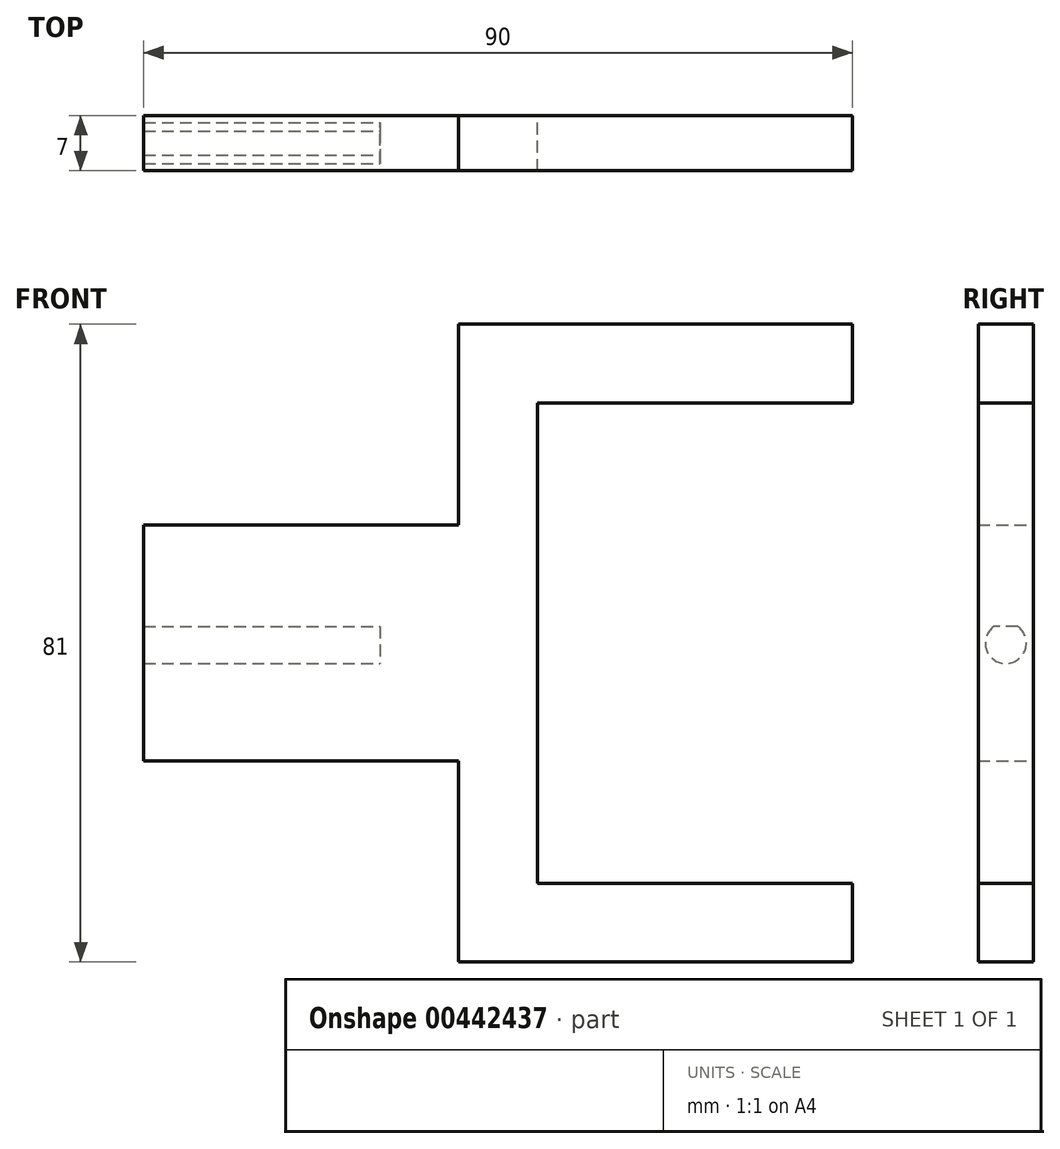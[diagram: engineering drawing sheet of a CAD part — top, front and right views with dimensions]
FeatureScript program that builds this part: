
annotation { "Feature Type Name" : "Feature", "Feature Type Description" : "" }
export const myFeature = defineFeature(function(context is Context, id is Id, definition is map)
    precondition{}
    {
        {
            var Q0;
            Q0=qCreatedBy(makeId("Front.planeOp"),FACE);
            var sketch = newSketch(context, id + "F0", { "sketchPlane" : qUnion([Q0])});
            skLineSegment(sketch, "E0.bottom", {"start": v(-40, 15) * mm, "end": v(0, 15) * mm});
            skLineSegment(sketch, "E0.top", {"start": v(-40, -15) * mm, "end": v(0, -15) * mm});
            skLineSegment(sketch, "E0.left", {"start": v(-40, 15) * mm, "end": v(-40, -15) * mm});
            skLineSegment(sketch, "E0.right", {"start": v(0, 15) * mm, "end": v(0, -15) * mm});
            skLineSegment(sketch, "E1.bottom", {"start": v(10, -40.5) * mm, "end": v(0, -40.5) * mm});
            skLineSegment(sketch, "E1.top", {"start": v(10, 40.5) * mm, "end": v(0, 40.5) * mm});
            skLineSegment(sketch, "E1.left", {"start": v(10, -40.5) * mm, "end": v(10, 40.5) * mm});
            skLineSegment(sketch, "E1.right", {"start": v(0, -40.5) * mm, "end": v(0, 40.5) * mm});
            skLineSegment(sketch, "E2.bottom", {"start": v(10, 40.5) * mm, "end": v(50, 40.5) * mm});
            skLineSegment(sketch, "E2.top", {"start": v(10, 30.5) * mm, "end": v(50, 30.5) * mm});
            skLineSegment(sketch, "E2.left", {"start": v(10, 40.5) * mm, "end": v(10, 30.5) * mm});
            skLineSegment(sketch, "E2.right", {"start": v(50, 40.5) * mm, "end": v(50, 30.5) * mm});
            skLineSegment(sketch, "E3.bottom", {"start": v(10, -40.5) * mm, "end": v(50, -40.5) * mm});
            skLineSegment(sketch, "E3.top", {"start": v(10, -30.5) * mm, "end": v(50, -30.5) * mm});
            skLineSegment(sketch, "E3.left", {"start": v(10, -40.5) * mm, "end": v(10, -30.5) * mm});
            skLineSegment(sketch, "E3.right", {"start": v(50, -40.5) * mm, "end": v(50, -30.5) * mm});
            skLineSegment(sketch, "E4", {"start": v(0, 0) * mm, "end": v(10, 0) * mm, "construction": true});
            skLineSegment(sketch, "E5", {"start": v(0, 0) * mm, "end": v(0, 0) * mm});
            skSolve(sketch);
        }
        {
            var Q0;
            Q0 = qSketchRegion(id + "F0", true);
            extrude(context, id + "F1", {"entities" : qUnion([Q0]), "endBound" : BoundingType.SYMMETRIC, "depth" : 7 * mm});
        }
        {
            var Q0;
            Q0=qCreatedBy(makeId("Right.planeOp"),FACE);
            var sketch = newSketch(context, id + "F2", { "sketchPlane" : qUnion([Q0])});
            skCircle(sketch, "E6", {"center": v(0, 0) * mm, "radius": 2.6 * mm});
            skLineSegment(sketch, "E7", {"start": v(1.53, 2.1) * mm, "end": v(-1.53, 2.1) * mm});
            skSolve(sketch);
        }
        {
            var Q0;
            {var subQ0=sQuery(id+"F2.wireOp",EDGE,"E7");Q0=makeQuery(id+"F2.imprint","IMPRINT",FACE,{"disambiguationData":[TD([[makeQuery(id+"F2.imprint","IMPRINT",EDGE,{"derivedFrom":subQ0}),1.0]])]});}
            extrude(context, id + "F3", {"entities" : qUnion([Q0]), "operationType" : NewBodyOperationType.REMOVE, "oppositeDirection" : true, "depth" : 40 * mm, "hasSecondDirection" : true, "secondDirectionOppositeDirection" : true, "secondDirectionDepth" : 10 * mm});
        }
    });
